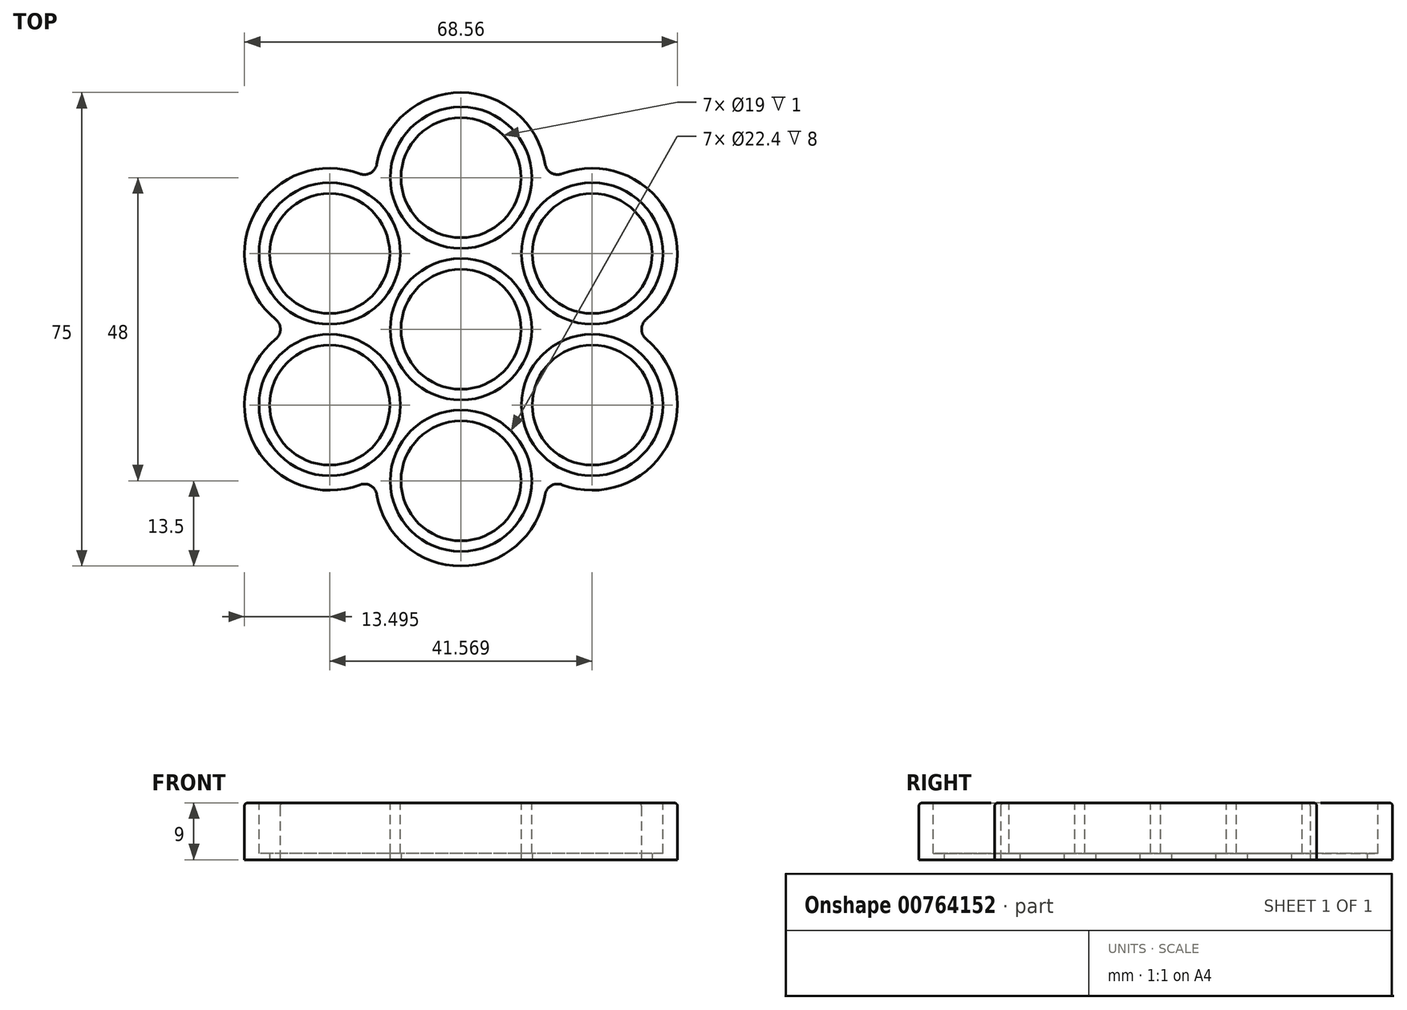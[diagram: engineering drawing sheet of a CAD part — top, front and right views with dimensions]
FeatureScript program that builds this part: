
annotation { "Feature Type Name" : "Feature", "Feature Type Description" : "" }
export const myFeature = defineFeature(function(context is Context, id is Id, definition is map)
    precondition{}
    {
        {
            var Q0;
            Q0=qCreatedBy(makeId("Top.planeOp"),FACE);
            var sketch = newSketch(context, id + "F0", { "sketchPlane" : qUnion([Q0])});
            skCircle(sketch, "E0", {"center": v(0, 0) * mm, "radius": 14 * mm});
            skCircle(sketch, "E1", {"center": v(0, 24) * mm, "radius": 13.5 * mm});
            skLineSegment(sketch, "E2", {"start": v(0, 24) * mm, "end": v(0, 0) * mm, "construction": true});
            skCircle(sketch, "E3", {"center": v(0, 24) * mm, "radius": 9.5 * mm});
            skCircle(sketch, "E4", {"center": v(0, 0) * mm, "radius": 9.5 * mm});
            skLineSegment(sketch, "E5.1.0", {"start": v(-20.78, 12) * mm, "end": v(0, 0) * mm, "construction": true});
            skCircle(sketch, "E5.1.1", {"center": v(-20.78, 12) * mm, "radius": 9.5 * mm});
            skCircle(sketch, "E5.1.3", {"center": v(-20.78, 12) * mm, "radius": 13.5 * mm});
            skLineSegment(sketch, "E5.2.0", {"start": v(-20.78, -12) * mm, "end": v(0, 0) * mm, "construction": true});
            skCircle(sketch, "E5.2.1", {"center": v(-20.78, -12) * mm, "radius": 9.5 * mm});
            skCircle(sketch, "E5.2.3", {"center": v(-20.78, -12) * mm, "radius": 13.5 * mm});
            skLineSegment(sketch, "E5.3.0", {"start": v(0, -24) * mm, "end": v(0, 0) * mm, "construction": true});
            skCircle(sketch, "E5.3.1", {"center": v(0, -24) * mm, "radius": 9.5 * mm});
            skCircle(sketch, "E5.3.3", {"center": v(0, -24) * mm, "radius": 13.5 * mm});
            skLineSegment(sketch, "E5.4.0", {"start": v(20.78, -12) * mm, "end": v(0, 0) * mm, "construction": true});
            skCircle(sketch, "E5.4.1", {"center": v(20.78, -12) * mm, "radius": 9.5 * mm});
            skCircle(sketch, "E5.4.3", {"center": v(20.78, -12) * mm, "radius": 13.5 * mm});
            skLineSegment(sketch, "E6.1.5.0", {"start": v(20.78, 12) * mm, "end": v(0, 0) * mm, "construction": true});
            skCircle(sketch, "E6.3.5.0", {"center": v(20.78, 12) * mm, "radius": 9.5 * mm});
            skCircle(sketch, "E6.7.5.0", {"center": v(20.78, 12) * mm, "radius": 13.5 * mm});
            skSolve(sketch);
        }
        {
            var Q0;
            Q0 = qSketchRegion(id + "F0", true);
            var Q1;
            Q1=makeQuery(id+"F0.imprint","IMPRINT",FACE,{"disambiguationData":[TD([[makeQuery(id+"F0.imprint","IMPRINT",EDGE,{"derivedFrom":sQuery(id+"F0.wireOp",EDGE,"E4")}),-1.0]])]});
            var Q2;
            {var subQ0=sQuery(id+"F0.wireOp",EDGE,"E5.2.3");var subQ1=sQuery(id+"F0.wireOp",EDGE,"E0");var subQ2=makeQuery(id+"F0.imprint","INTERSECT",VERTEX,{"disambiguationData":[OD(0.0)],"derivedFrom":[subQ1,subQ0]});Q2=makeQuery(id+"F0.imprint","IMPRINT",FACE,{"disambiguationData":[TD([[makeQuery(id+"F0.imprint","IMPRINT",EDGE,{"disambiguationData":[TD([[subQ2,-1.0]])],"derivedFrom":subQ1}),1.0]])]});}
            var Q3;
            {var subQ0=sQuery(id+"F0.wireOp",EDGE,"E5.1.3");var subQ1=sQuery(id+"F0.wireOp",EDGE,"E0");var subQ2=makeQuery(id+"F0.imprint","INTERSECT",VERTEX,{"disambiguationData":[OD(0.0)],"derivedFrom":[subQ1,subQ0]});Q3=makeQuery(id+"F0.imprint","IMPRINT",FACE,{"disambiguationData":[TD([[makeQuery(id+"F0.imprint","IMPRINT",EDGE,{"disambiguationData":[TD([[subQ2,-1.0]])],"derivedFrom":subQ1}),1.0]])]});}
            var Q4;
            {var subQ0=sQuery(id+"F0.wireOp",EDGE,"E1");var subQ1=sQuery(id+"F0.wireOp",EDGE,"E0");var subQ2=makeQuery(id+"F0.imprint","INTERSECT",VERTEX,{"disambiguationData":[OD(0.0)],"derivedFrom":[subQ1,subQ0]});Q4=makeQuery(id+"F0.imprint","IMPRINT",FACE,{"disambiguationData":[TD([[makeQuery(id+"F0.imprint","IMPRINT",EDGE,{"disambiguationData":[TD([[subQ2,-1.0]])],"derivedFrom":subQ1}),1.0]])]});}
            var Q5;
            {var subQ0=sQuery(id+"F0.wireOp",EDGE,"E6.7.5.0");var subQ1=sQuery(id+"F0.wireOp",EDGE,"E0");var subQ2=makeQuery(id+"F0.imprint","INTERSECT",VERTEX,{"disambiguationData":[OD(0.0)],"derivedFrom":[subQ1,subQ0]});Q5=makeQuery(id+"F0.imprint","IMPRINT",FACE,{"disambiguationData":[TD([[makeQuery(id+"F0.imprint","IMPRINT",EDGE,{"disambiguationData":[TD([[subQ2,1.0]])],"derivedFrom":subQ1}),1.0]])]});}
            var Q6;
            {var subQ0=sQuery(id+"F0.wireOp",EDGE,"E5.4.3");var subQ1=sQuery(id+"F0.wireOp",EDGE,"E0");var subQ2=makeQuery(id+"F0.imprint","INTERSECT",VERTEX,{"disambiguationData":[OD(0.0)],"derivedFrom":[subQ1,subQ0]});Q6=makeQuery(id+"F0.imprint","IMPRINT",FACE,{"disambiguationData":[TD([[makeQuery(id+"F0.imprint","IMPRINT",EDGE,{"disambiguationData":[TD([[subQ2,-1.0]])],"derivedFrom":subQ1}),1.0]])]});}
            var Q7;
            {var subQ0=sQuery(id+"F0.wireOp",EDGE,"E5.3.3");var subQ1=sQuery(id+"F0.wireOp",EDGE,"E0");var subQ2=makeQuery(id+"F0.imprint","INTERSECT",VERTEX,{"disambiguationData":[OD(0.0)],"derivedFrom":[subQ1,subQ0]});Q7=makeQuery(id+"F0.imprint","IMPRINT",FACE,{"disambiguationData":[TD([[makeQuery(id+"F0.imprint","IMPRINT",EDGE,{"disambiguationData":[TD([[subQ2,-1.0]])],"derivedFrom":subQ1}),1.0]])]});}
            var Q8;
            {var subQ0=sQuery(id+"F0.wireOp",EDGE,"E5.2.3");var subQ1=sQuery(id+"F0.wireOp",EDGE,"E0");var subQ2=makeQuery(id+"F0.imprint","INTERSECT",VERTEX,{"disambiguationData":[OD(1.0)],"derivedFrom":[subQ1,subQ0]});Q8=makeQuery(id+"F0.imprint","IMPRINT",FACE,{"disambiguationData":[TD([[makeQuery(id+"F0.imprint","IMPRINT",EDGE,{"disambiguationData":[TD([[subQ2,-1.0]])],"derivedFrom":subQ1}),-1.0]])]});}
            var Q9;
            {var subQ0=sQuery(id+"F0.wireOp",EDGE,"E5.3.3");var subQ1=sQuery(id+"F0.wireOp",EDGE,"E0");var subQ2=makeQuery(id+"F0.imprint","INTERSECT",VERTEX,{"disambiguationData":[OD(1.0)],"derivedFrom":[subQ1,subQ0]});Q9=makeQuery(id+"F0.imprint","IMPRINT",FACE,{"disambiguationData":[TD([[makeQuery(id+"F0.imprint","IMPRINT",EDGE,{"disambiguationData":[TD([[subQ2,-1.0]])],"derivedFrom":subQ1}),-1.0]])]});}
            var Q10;
            {var subQ0=sQuery(id+"F0.wireOp",EDGE,"E6.7.5.0");var subQ1=sQuery(id+"F0.wireOp",EDGE,"E0");var subQ2=makeQuery(id+"F0.imprint","INTERSECT",VERTEX,{"disambiguationData":[OD(1.0)],"derivedFrom":[subQ1,subQ0]});Q10=makeQuery(id+"F0.imprint","IMPRINT",FACE,{"disambiguationData":[TD([[makeQuery(id+"F0.imprint","IMPRINT",EDGE,{"disambiguationData":[TD([[subQ2,1.0]])],"derivedFrom":subQ1}),-1.0]])]});}
            var Q11;
            {var subQ0=sQuery(id+"F0.wireOp",EDGE,"E6.7.5.0");var subQ1=sQuery(id+"F0.wireOp",EDGE,"E0");var subQ2=makeQuery(id+"F0.imprint","INTERSECT",VERTEX,{"disambiguationData":[OD(0.0)],"derivedFrom":[subQ1,subQ0]});Q11=makeQuery(id+"F0.imprint","IMPRINT",FACE,{"disambiguationData":[TD([[makeQuery(id+"F0.imprint","IMPRINT",EDGE,{"disambiguationData":[TD([[subQ2,-1.0]])],"derivedFrom":subQ1}),-1.0]])]});}
            var Q12;
            {var subQ0=sQuery(id+"F0.wireOp",EDGE,"E1");var subQ1=sQuery(id+"F0.wireOp",EDGE,"E0");var subQ2=makeQuery(id+"F0.imprint","INTERSECT",VERTEX,{"disambiguationData":[OD(1.0)],"derivedFrom":[subQ1,subQ0]});Q12=makeQuery(id+"F0.imprint","IMPRINT",FACE,{"disambiguationData":[TD([[makeQuery(id+"F0.imprint","IMPRINT",EDGE,{"disambiguationData":[TD([[subQ2,-1.0]])],"derivedFrom":subQ1}),-1.0]])]});}
            var Q13;
            {var subQ0=sQuery(id+"F0.wireOp",EDGE,"E5.1.3");var subQ1=sQuery(id+"F0.wireOp",EDGE,"E0");var subQ2=makeQuery(id+"F0.imprint","INTERSECT",VERTEX,{"disambiguationData":[OD(1.0)],"derivedFrom":[subQ1,subQ0]});Q13=makeQuery(id+"F0.imprint","IMPRINT",FACE,{"disambiguationData":[TD([[makeQuery(id+"F0.imprint","IMPRINT",EDGE,{"disambiguationData":[TD([[subQ2,-1.0]])],"derivedFrom":subQ1}),-1.0]])]});}
            extrude(context, id + "F1", {"entities" : qUnion([Q0, Q1, Q2, Q3, Q4, Q5, Q6, Q7, Q8, Q9, Q10, Q11, Q12, Q13]), "depth" : 9 * mm, "offsetDistance" : 25 * mm});
        }
        {
            var Q0;
            Q0=makeQuery(id+"F1.opExtrude","CAP_FACE",FACE,{"disambiguationData":[OSD([sQuery(id+"F0.wireOp",EDGE,"E1"),sQuery(id+"F0.wireOp",EDGE,"E3"),sQuery(id+"F0.wireOp",EDGE,"E4"),sQuery(id+"F0.wireOp",EDGE,"E5.1.1"),sQuery(id+"F0.wireOp",EDGE,"E5.1.3"),sQuery(id+"F0.wireOp",EDGE,"E5.2.1"),sQuery(id+"F0.wireOp",EDGE,"E5.2.3"),sQuery(id+"F0.wireOp",EDGE,"E5.3.1"),sQuery(id+"F0.wireOp",EDGE,"E5.3.3"),sQuery(id+"F0.wireOp",EDGE,"E5.4.1"),sQuery(id+"F0.wireOp",EDGE,"E5.4.3"),sQuery(id+"F0.wireOp",EDGE,"E6.3.5.0"),sQuery(id+"F0.wireOp",EDGE,"E6.7.5.0")])],"isStart":false});
            var sketch = newSketch(context, id + "F2", { "sketchPlane" : qUnion([Q0])});
            skCircle(sketch, "E7.0", {"center": v(0, 24) * mm, "radius": 9.5 * mm, "construction": true});
            skCircle(sketch, "E8.0", {"center": v(20.78, 12) * mm, "radius": 9.5 * mm, "construction": true});
            skCircle(sketch, "E9.0", {"center": v(0, 0) * mm, "radius": 9.5 * mm, "construction": true});
            skCircle(sketch, "E10.0", {"center": v(20.78, -12) * mm, "radius": 9.5 * mm, "construction": true});
            skCircle(sketch, "E11.0", {"center": v(0, -24) * mm, "radius": 9.5 * mm, "construction": true});
            skCircle(sketch, "E12.0", {"center": v(-20.78, -12) * mm, "radius": 9.5 * mm, "construction": true});
            skCircle(sketch, "E13.0", {"center": v(-20.78, 12) * mm, "radius": 9.5 * mm, "construction": true});
            skCircle(sketch, "E14", {"center": v(0, 0) * mm, "radius": 11.2 * mm});
            skCircle(sketch, "E15", {"center": v(0, 24) * mm, "radius": 11.2 * mm});
            skCircle(sketch, "E16", {"center": v(20.78, 12) * mm, "radius": 11.2 * mm});
            skCircle(sketch, "E17", {"center": v(20.78, -12) * mm, "radius": 11.2 * mm});
            skCircle(sketch, "E18", {"center": v(0, -24) * mm, "radius": 11.2 * mm});
            skCircle(sketch, "E19", {"center": v(-20.78, -12) * mm, "radius": 11.2 * mm});
            skCircle(sketch, "E20", {"center": v(-20.78, 12) * mm, "radius": 11.2 * mm});
            skSolve(sketch);
        }
        {
            var Q0;
            Q0 = qSketchRegion(id + "F2", true);
            extrude(context, id + "F3", {"entities" : qUnion([Q0]), "operationType" : NewBodyOperationType.REMOVE, "oppositeDirection" : true, "depth" : 8 * mm, "offsetDistance" : 25 * mm});
        }
        {
            var Q0;
            Q0=makeQuery(id+"F1.opExtrude","SWEPT_EDGE",EDGE,{"disambiguationData":[OSD([sQuery(id+"F0.wireOp",EDGE,"E5.2.3"),sQuery(id+"F0.wireOp",EDGE,"E5.3.3")])]});
            var Q1;
            Q1=makeQuery(id+"F1.opExtrude","SWEPT_EDGE",EDGE,{"disambiguationData":[OSD([sQuery(id+"F0.wireOp",EDGE,"E5.3.3"),sQuery(id+"F0.wireOp",EDGE,"E5.4.3")])]});
            var Q2;
            Q2=makeQuery(id+"F1.opExtrude","SWEPT_EDGE",EDGE,{"disambiguationData":[OSD([sQuery(id+"F0.wireOp",EDGE,"E5.4.3"),sQuery(id+"F0.wireOp",EDGE,"E6.7.5.0")])]});
            var Q3;
            Q3=makeQuery(id+"F1.opExtrude","SWEPT_EDGE",EDGE,{"disambiguationData":[OSD([sQuery(id+"F0.wireOp",EDGE,"E1"),sQuery(id+"F0.wireOp",EDGE,"E6.7.5.0")])]});
            var Q4;
            Q4=makeQuery(id+"F1.opExtrude","SWEPT_EDGE",EDGE,{"disambiguationData":[OSD([sQuery(id+"F0.wireOp",EDGE,"E1"),sQuery(id+"F0.wireOp",EDGE,"E5.1.3")])]});
            var Q5;
            Q5=makeQuery(id+"F1.opExtrude","SWEPT_EDGE",EDGE,{"disambiguationData":[OSD([sQuery(id+"F0.wireOp",EDGE,"E5.1.3"),sQuery(id+"F0.wireOp",EDGE,"E5.2.3")])]});
            fillet(context, id + "F4", {"entities" : qUnion([Q0, Q1, Q2, Q3, Q4, Q5]), "radius" : 2 * mm, "tangentPropagation" : true, "allowEdgeOverflow" : false});
        }
        {
            var Q0;
            Q0=makeQuery(id+"F1.opExtrude","CAP_EDGE",EDGE,{"disambiguationData":[OSD([sQuery(id+"F0.wireOp",EDGE,"E5.2.3")])],"isStart":false});
            var Q1;
            Q1=makeQuery(id+"F3.boolean.opBoolean","COPY",EDGE,{"derivedFrom":makeQuery(id+"F3.opExtrude","CAP_EDGE",EDGE,{"disambiguationData":[OSD([sQuery(id+"F2.wireOp",EDGE,"E19")])],"isStart":true})});
            var Q2;
            Q2=makeQuery(id+"F3.boolean.opBoolean","COPY",EDGE,{"derivedFrom":makeQuery(id+"F3.opExtrude","CAP_EDGE",EDGE,{"disambiguationData":[OSD([sQuery(id+"F2.wireOp",EDGE,"E14")])],"isStart":true})});
            var Q3;
            Q3=makeQuery(id+"F3.boolean.opBoolean","COPY",EDGE,{"derivedFrom":makeQuery(id+"F3.opExtrude","CAP_EDGE",EDGE,{"disambiguationData":[OSD([sQuery(id+"F2.wireOp",EDGE,"E20")])],"isStart":true})});
            var Q4;
            Q4=makeQuery(id+"F3.boolean.opBoolean","COPY",EDGE,{"derivedFrom":makeQuery(id+"F3.opExtrude","CAP_EDGE",EDGE,{"disambiguationData":[OSD([sQuery(id+"F2.wireOp",EDGE,"E15")])],"isStart":true})});
            var Q5;
            Q5=makeQuery(id+"F3.boolean.opBoolean","COPY",EDGE,{"derivedFrom":makeQuery(id+"F3.opExtrude","CAP_EDGE",EDGE,{"disambiguationData":[OSD([sQuery(id+"F2.wireOp",EDGE,"E16")])],"isStart":true})});
            var Q6;
            Q6=makeQuery(id+"F3.boolean.opBoolean","COPY",EDGE,{"derivedFrom":makeQuery(id+"F3.opExtrude","CAP_EDGE",EDGE,{"disambiguationData":[OSD([sQuery(id+"F2.wireOp",EDGE,"E17")])],"isStart":true})});
            var Q7;
            Q7=makeQuery(id+"F3.boolean.opBoolean","COPY",EDGE,{"derivedFrom":makeQuery(id+"F3.opExtrude","CAP_EDGE",EDGE,{"disambiguationData":[OSD([sQuery(id+"F2.wireOp",EDGE,"E18")])],"isStart":true})});
            fillet(context, id + "F5", {"entities" : qUnion([Q0, Q1, Q2, Q3, Q4, Q5, Q6, Q7]), "radius" : .5 * mm, "tangentPropagation" : true, "allowEdgeOverflow" : false});
        }
    });
